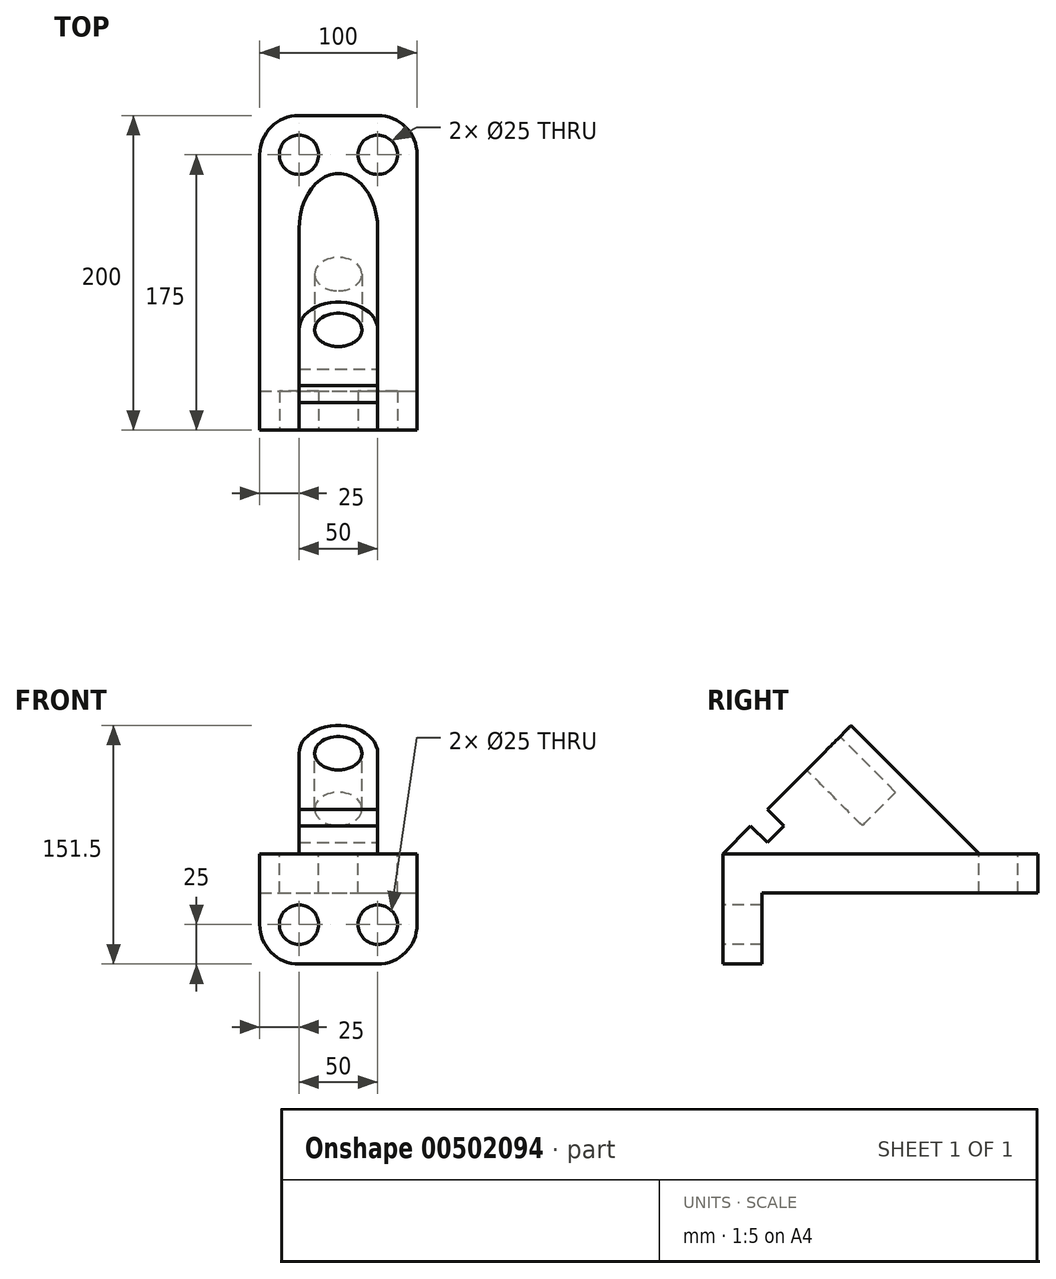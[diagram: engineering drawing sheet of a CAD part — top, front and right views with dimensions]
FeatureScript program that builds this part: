
annotation { "Feature Type Name" : "Feature", "Feature Type Description" : "" }
export const myFeature = defineFeature(function(context is Context, id is Id, definition is map)
    precondition{}
    {
        {
            var Q0;
            Q0=qCreatedBy(makeId("Front.planeOp"),FACE);
            var sketch = newSketch(context, id + "F0", { "sketchPlane" : qUnion([Q0])});
            skLineSegment(sketch, "E0.bottom", {"start": v(0, 0) * mm, "end": v(100, 0) * mm});
            skLineSegment(sketch, "E0.top", {"start": v(0, -70) * mm, "end": v(100, -70) * mm});
            skLineSegment(sketch, "E0.left", {"start": v(0, 0) * mm, "end": v(0, -70) * mm});
            skLineSegment(sketch, "E0.right", {"start": v(100, 0) * mm, "end": v(100, -70) * mm});
            skSolve(sketch);
        }
        {
            var Q0;
            Q0=makeQuery(id+"F0.imprint","IMPRINT",FACE,{"disambiguationData":[TD([[makeQuery(id+"F0.imprint","IMPRINT",EDGE,{"derivedFrom":sQuery(id+"F0.wireOp",EDGE,"E0.bottom")}),-1.0]])]});
            extrude(context, id + "F1", {"entities" : qUnion([Q0]), "oppositeDirection" : true, "depth" : 200 * mm, "offsetDistance" : 25 * mm});
        }
        {
            var Q0;
            Q0=makeQuery(id+"F1.opExtrude","SWEPT_EDGE",EDGE,{"disambiguationData":[OSD([sQuery(id+"F0.wireOp",EDGE,"E0.top"),sQuery(id+"F0.wireOp",EDGE,"E0.right")])]});
            var Q1;
            Q1=makeQuery(id+"F1.opExtrude","SWEPT_EDGE",EDGE,{"disambiguationData":[OSD([sQuery(id+"F0.wireOp",EDGE,"E0.top"),sQuery(id+"F0.wireOp",EDGE,"E0.left")])]});
            var Q2;
            Q2=makeQuery(id+"F1.opExtrude","CAP_EDGE",EDGE,{"disambiguationData":[OSD([sQuery(id+"F0.wireOp",EDGE,"E0.right")])],"isStart":false});
            var Q3;
            Q3=makeQuery(id+"F1.opExtrude","CAP_EDGE",EDGE,{"disambiguationData":[OSD([sQuery(id+"F0.wireOp",EDGE,"E0.left")])],"isStart":false});
            fillet(context, id + "F2", {"entities" : qUnion([Q0, Q1, Q2, Q3]), "radius" : 25 * mm, "tangentPropagation" : true, "allowEdgeOverflow" : false});
        }
        {
            var Q0;
            Q0=makeQuery(id+"F1.opExtrude","SWEPT_FACE",FACE,{"disambiguationData":[OSD([sQuery(id+"F0.wireOp",EDGE,"E0.right")])]});
            var Q1;
            Q1=makeQuery(id+"F1.opExtrude","CAP_FACE",FACE,{"disambiguationData":[OSD([sQuery(id+"F0.wireOp",EDGE,"E0.bottom"),sQuery(id+"F0.wireOp",EDGE,"E0.top"),sQuery(id+"F0.wireOp",EDGE,"E0.left"),sQuery(id+"F0.wireOp",EDGE,"E0.right")])],"isStart":false});
            var Q2;
            Q2=makeQuery(id+"F2.opFillet","BLEND_FACE",FACE,{"disambiguationData":[OSD([sQuery(id+"F0.wireOp",EDGE,"E0.right")])]});
            var Q3;
            Q3=makeQuery(id+"F2.opFillet","BLEND_FACE",FACE,{"disambiguationData":[OSD([sQuery(id+"F0.wireOp",EDGE,"E0.left")])]});
            var Q4;
            Q4=makeQuery(id+"F1.opExtrude","SWEPT_FACE",FACE,{"disambiguationData":[OSD([sQuery(id+"F0.wireOp",EDGE,"E0.left")])]});
            var Q5;
            Q5=makeQuery(id+"F2.opFillet","BLEND_FACE",FACE,{"disambiguationData":[OSD([sQuery(id+"F0.wireOp",EDGE,"E0.top"),sQuery(id+"F0.wireOp",EDGE,"E0.right")])]});
            var Q6;
            Q6=makeQuery(id+"F1.opExtrude","SWEPT_FACE",FACE,{"disambiguationData":[OSD([sQuery(id+"F0.wireOp",EDGE,"E0.top")])]});
            var Q7;
            Q7=makeQuery(id+"F2.opFillet","BLEND_FACE",FACE,{"disambiguationData":[OSD([sQuery(id+"F0.wireOp",EDGE,"E0.top"),sQuery(id+"F0.wireOp",EDGE,"E0.left")])]});
            shell(context, id + "F3", {"entities" : qUnion([Q0, Q1, Q2, Q3, Q4, Q5, Q6, Q7]), "thickness" : 25 * mm});
        }
        {
            var Q0;
            Q0=makeQuery(id+"F1.opExtrude","SWEPT_FACE",FACE,{"disambiguationData":[OSD([sQuery(id+"F0.wireOp",EDGE,"E0.right")])]});
            var sketch = newSketch(context, id + "F4", { "sketchPlane" : qUnion([Q0])});
            skLineSegment(sketch, "E1", {"start": v(0, 0) * mm, "end": v(17.68, 17.68) * mm});
            skLineSegment(sketch, "E2", {"start": v(81.5, 81.5) * mm, "end": v(163, 0) * mm});
            skLineSegment(sketch, "E3", {"start": v(0, 0) * mm, "end": v(163, 0) * mm});
            skLineSegment(sketch, "E4", {"start": v(17.68, 17.68) * mm, "end": v(28.28, 7.07) * mm});
            skLineSegment(sketch, "E5", {"start": v(28.28, 7.07) * mm, "end": v(38.9, 17.68) * mm});
            skLineSegment(sketch, "E6", {"start": v(38.9, 17.68) * mm, "end": v(28.28, 28.28) * mm});
            skLineSegment(sketch, "E7.trimOffspring", {"start": v(28.28, 28.28) * mm, "end": v(81.5, 81.5) * mm});
            skSolve(sketch);
        }
        {
            var Q0;
            Q0=qSketchRegion(id+"F4",true);
            extrude(context, id + "F5", {"entities" : qUnion([Q0]), "operationType" : NewBodyOperationType.ADD, "oppositeDirection" : true, "depth" : 75 * mm, "offsetDistance" : 25 * mm, "hasSecondDirection" : true, "secondDirectionOppositeDirection" : true, "secondDirectionDepth" : 25 * mm});
        }
        {
            var Q0;
            Q0=makeQuery(id+"F5.opExtrude","CAP_EDGE",EDGE,{"disambiguationData":[OSD([sQuery(id+"F4.wireOp",EDGE,"E2")])],"isStart":true});
            var Q1;
            Q1=makeQuery(id+"F5.opExtrude","CAP_EDGE",EDGE,{"disambiguationData":[OSD([sQuery(id+"F4.wireOp",EDGE,"E2")])],"isStart":false});
            fillet(context, id + "F6", {"entities" : qUnion([Q0, Q1]), "radius" : 25 * mm, "tangentPropagation" : true, "allowEdgeOverflow" : false});
        }
        {
            var Q0;
            Q0=makeQuery(id+"F1.opExtrude","CAP_FACE",FACE,{"disambiguationData":[OSD([sQuery(id+"F0.wireOp",EDGE,"E0.bottom"),sQuery(id+"F0.wireOp",EDGE,"E0.top"),sQuery(id+"F0.wireOp",EDGE,"E0.left"),sQuery(id+"F0.wireOp",EDGE,"E0.right")])],"isStart":true});
            var sketch = newSketch(context, id + "F7", { "sketchPlane" : qUnion([Q0])});
            skPoint(sketch, "E8", {"position": v(75, -45) * mm});
            skPoint(sketch, "E9", {"position": v(25, -45) * mm});
            skSolve(sketch);
        }
        {
            var Q0;
            Q0=makeQuery(id+"F1.opExtrude","SWEPT_FACE",FACE,{"disambiguationData":[OSD([sQuery(id+"F0.wireOp",EDGE,"E0.bottom")])]});
            var sketch = newSketch(context, id + "F8", { "sketchPlane" : qUnion([Q0])});
            skPoint(sketch, "E10", {"position": v(75, 175) * mm});
            skPoint(sketch, "E11", {"position": v(25, 175) * mm});
            skSolve(sketch);
        }
        {
            var Q0;
            Q0=sQuery(id+"F7.wireOp",VERTEX,"E8");
            var Q1;
            Q1=sQuery(id+"F7.wireOp",VERTEX,"E9");
            var Q2;
            Q2=sQuery(id+"F8.wireOp",VERTEX,"E10");
            var Q3;
            Q3=sQuery(id+"F8.wireOp",VERTEX,"E11");
            var Q4;
            Q4=makeQuery(id+"F1.opExtrude","SWEPT_BODY",BODY,{"disambiguationData":[OSD([sQuery(id+"F0.wireOp",EDGE,"E0.bottom"),sQuery(id+"F0.wireOp",EDGE,"E0.top"),sQuery(id+"F0.wireOp",EDGE,"E0.left"),sQuery(id+"F0.wireOp",EDGE,"E0.right")])]});
            hole(context, id + "F9", {"style" : HoleStyle.SIMPLE, "endStyle" : HoleEndStyle.BLIND, "holeDiameter" : 25 * mm, "majorDiameter" : 5 * mm, "holeDepth" : 100 * mm, "isTappedThrough" : true, "tappedDepth" : 12 * mm, "tapClearance" : 3, "startFromSketch" : true, "locations" : qUnion([Q0, Q1, Q2, Q3]), "scope" : qUnion([Q4])});
        }
        {
            var Q0;
            Q0=makeQuery(id+"F5.opExtrude","SWEPT_FACE",FACE,{"disambiguationData":[OSD([sQuery(id+"F4.wireOp",EDGE,"E7.trimOffspring")])]});
            var sketch = newSketch(context, id + "F10", { "sketchPlane" : qUnion([Q0])});
            skPoint(sketch, "E12", {"position": v(50, 90.26) * mm});
            skCircle(sketch, "E13", {"center": v(50, 90.26) * mm, "radius": 15 * mm});
            skSolve(sketch);
        }
        {
            var Q0;
            Q0=makeQuery(id+"F10.imprint","IMPRINT",FACE,{"disambiguationData":[TD([[makeQuery(id+"F10.imprint","IMPRINT",EDGE,{"derivedFrom":sQuery(id+"F10.wireOp",EDGE,"E13")}),1.0]])]});
            extrude(context, id + "F11", {"entities" : qUnion([Q0]), "operationType" : NewBodyOperationType.REMOVE, "oppositeDirection" : true, "depth" : 50 * mm, "offsetDistance" : 25 * mm});
        }
    });
